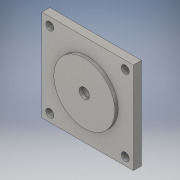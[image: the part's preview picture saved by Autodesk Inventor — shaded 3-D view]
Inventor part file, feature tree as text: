
AUTODESK INVENTOR PART (.ipt)
format: ipt  version: 2016 (Build 200138000, 138)  size: 131,584 bytes
history: native  units: in
note: dims shown in document units (in); Inventor stores cm internally (conversion verified against a paired STEP export)
features: extrude x2, sketch x2
ambient origin geometry x8: Origin, YZ Plane, XZ Plane, XY Plane, X Axis, Y Axis, Z Axis, Center Point
bodies: Solid1 (feature_tree)
feature tree (4):
  extrude  "Extrusion1"  Depth=2.2441in
  extrude  "Extrusion2"  Depth=0.0787in
  sketch  "Sketch1"  dims[d0=2.2441in d1=2.2441in]
  sketch  "Sketch2"  dims[d2=1.122in d3=1.122in d4=0.1969in d5=0.1969in d6=0.1969in d7=0.1969in d8=0.1969in d9=0.1969in d10=0.1969in d11=0.1969in d12=0.1969in d13=0.1969in d14=0.1969in d15=0.1969in d16=0.252in d17=0.1969in d18=0.0in d19=1.4961in d20=0.0787in d21=0.0in]
